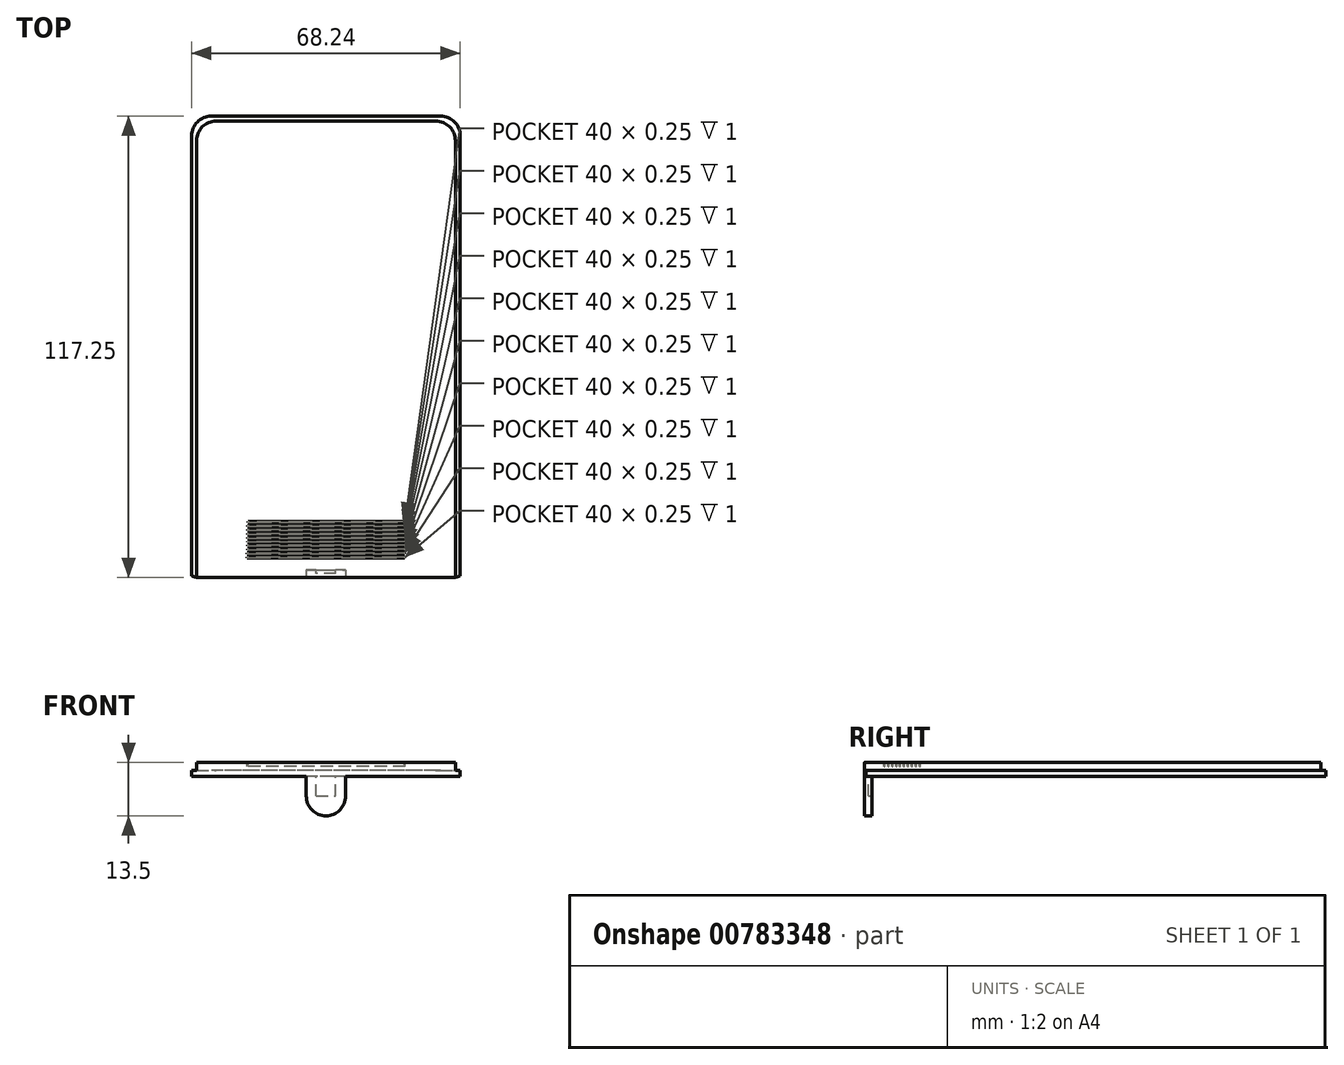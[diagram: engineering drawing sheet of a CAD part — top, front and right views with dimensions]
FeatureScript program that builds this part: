
annotation { "Feature Type Name" : "Feature", "Feature Type Description" : "" }
export const myFeature = defineFeature(function(context is Context, id is Id, definition is map)
    precondition{}
    {
        {
            var Q0;
            Q0=qCreatedBy(makeId("Front.planeOp"),FACE);
            var sketch = newSketch(context, id + "F0", { "sketchPlane" : qUnion([Q0])});
            skLineSegment(sketch, "E0.top", {"start": v(32.88, 3.5) * mm, "end": v(-32.87, 3.5) * mm});
            skLineSegment(sketch, "E0.left", {"start": v(32.88, 1.5) * mm, "end": v(32.88, 3.5) * mm});
            skLineSegment(sketch, "E0.right", {"start": v(-32.87, 1.5) * mm, "end": v(-32.87, 3.5) * mm});
            skLineSegment(sketch, "E1.bottom", {"start": v(34.12, 0) * mm, "end": v(-34.12, 0) * mm});
            skLineSegment(sketch, "E1.left", {"start": v(34.13, 0) * mm, "end": v(34.13, 1.5) * mm});
            skLineSegment(sketch, "E1.right", {"start": v(-34.12, 0) * mm, "end": v(-34.12, 1.5) * mm});
            skLineSegment(sketch, "E2", {"start": v(0, 3.25) * mm, "end": v(0, 44.31) * mm, "construction": true});
            skLineSegment(sketch, "E3", {"start": v(-34.12, 1.5) * mm, "end": v(-32.87, 1.5) * mm});
            skLineSegment(sketch, "E4", {"start": v(32.88, 1.5) * mm, "end": v(34.13, 1.5) * mm});
            skSolve(sketch);
        }
        {
            var Q0;
            Q0=makeQuery(id+"F0.imprint","IMPRINT",FACE,{"disambiguationData":[TD([[makeQuery(id+"F0.imprint","IMPRINT",EDGE,{"derivedFrom":sQuery(id+"F0.wireOp",EDGE,"E0.top")}),1.0]])]});
            extrude(context, id + "F1", {"entities" : qUnion([Q0]), "oppositeDirection" : true, "depth" : (106 + 10) * mm, "offsetDistance" : 25 * mm});
        }
        {
            var Q0;
            Q0=makeQuery(id+"F1.opExtrude","CAP_FACE",FACE,{"disambiguationData":[OSD([sQuery(id+"F0.wireOp",EDGE,"E0.top"),sQuery(id+"F0.wireOp",EDGE,"E0.left"),sQuery(id+"F0.wireOp",EDGE,"E0.right"),sQuery(id+"F0.wireOp",EDGE,"E1.bottom"),sQuery(id+"F0.wireOp",EDGE,"E1.left"),sQuery(id+"F0.wireOp",EDGE,"E1.right"),sQuery(id+"F0.wireOp",EDGE,"E3"),sQuery(id+"F0.wireOp",EDGE,"E4")])],"isStart":false});
            var sketch = newSketch(context, id + "F2", { "sketchPlane" : qUnion([Q0])});
            skLineSegment(sketch, "E5.bottom", {"start": v(-34.13, 1.5) * mm, "end": v(34.12, 1.5) * mm});
            skLineSegment(sketch, "E5.top", {"start": v(-34.13, 0) * mm, "end": v(34.12, 0) * mm});
            skLineSegment(sketch, "E5.left", {"start": v(-34.13, 1.5) * mm, "end": v(-34.13, 0) * mm});
            skLineSegment(sketch, "E5.right", {"start": v(34.12, 1.5) * mm, "end": v(34.12, 0) * mm});
            skSolve(sketch);
        }
        {
            var Q0;
            Q0=qSketchRegion(id+"F2",true);
            extrude(context, id + "F3", {"entities" : qUnion([Q0]), "operationType" : NewBodyOperationType.ADD, "depth" : 1.25 * mm, "offsetDistance" : 25 * mm});
        }
        {
            var Q0;
            Q0=makeQuery(id+"F3.opExtrude","CAP_EDGE",EDGE,{"disambiguationData":[OSD([sQuery(id+"F2.wireOp",EDGE,"E5.left")])],"isStart":false});
            var Q1;
            Q1=makeQuery(id+"F3.opExtrude","CAP_EDGE",EDGE,{"disambiguationData":[OSD([sQuery(id+"F2.wireOp",EDGE,"E5.right")])],"isStart":false});
            var Q2;
            Q2=makeQuery(id+"F1.opExtrude","CAP_EDGE",EDGE,{"disambiguationData":[OSD([sQuery(id+"F0.wireOp",EDGE,"E0.right")])],"isStart":false});
            var Q3;
            Q3=makeQuery(id+"F1.opExtrude","CAP_EDGE",EDGE,{"disambiguationData":[OSD([sQuery(id+"F0.wireOp",EDGE,"E0.left")])],"isStart":false});
            fillet(context, id + "F4", {"entities" : qUnion([Q0, Q1, Q2, Q3]), "radius" : 5 * mm, "tangentPropagation" : true, "allowEdgeOverflow" : false});
        }
        {
            var Q0;
            Q0=qCreatedBy(makeId("Top.planeOp"),FACE);
            var sketch = newSketch(context, id + "F5", { "sketchPlane" : qUnion([Q0])});
            skLineSegment(sketch, "E6.0.0", {"start": v(-34.12, 73) * mm, "end": v(34.12, 73) * mm, "construction": true});
            skLineSegment(sketch, "E6.0.1", {"start": v(34.12, 73) * mm, "end": v(34.12, 5) * mm, "construction": true});
            skLineSegment(sketch, "E6.0.2", {"start": v(29.12, 0) * mm, "end": v(-29.12, 0) * mm, "construction": true});
            skLineSegment(sketch, "E6.0.3", {"start": v(-34.12, 5) * mm, "end": v(-34.12, 73) * mm, "construction": true});
            skPoint(sketch, "E7.middle", {"position": v(-2.88, 36.5) * mm});
            skPoint(sketch, "E8.visualSharp", {"position": v(-37, 0) * mm});
            skArc(sketch, "E8.filletArc", {"start": v(-37, 5) * mm, "mid": v(-35.54, 1.46) * mm, "end": v(-32, 0) * mm, "construction": true});
            skPoint(sketch, "E9.visualSharp", {"position": v(37, 0) * mm});
            skArc(sketch, "E9.filletArc", {"start": v(32, 0) * mm, "mid": v(35.54, 1.46) * mm, "end": v(37, 5) * mm, "construction": true});
            skArc(sketch, "E10", {"start": v(-37, 5) * mm, "mid": v(-35.54, 1.46) * mm, "end": v(-32, 0) * mm});
            skLineSegment(sketch, "E11", {"start": v(-32.48, -8.24) * mm, "end": v(-32, 0) * mm});
            skLineSegment(sketch, "E12", {"start": v(-37, 5) * mm, "end": v(-47.45, 5.13) * mm});
            skLineSegment(sketch, "E13", {"start": v(0, 0) * mm, "end": v(0, 9.43) * mm, "construction": true});
            skLineSegment(sketch, "E14.MirrorCS", {"start": v(37, 5) * mm, "end": v(47.87, 4.85) * mm});
            skLineSegment(sketch, "E15.MirrorCS", {"start": v(31.7, -9.05) * mm, "end": v(32, 0) * mm});
            skPoint(sketch, "E16.MirrorP", {"position": v(31.25, 0) * mm});
            skLineSegment(sketch, "E17", {"start": v(-47.45, 5.13) * mm, "end": v(-32.48, -8.24) * mm});
            skLineSegment(sketch, "E18", {"start": v(31.7, -9.05) * mm, "end": v(47.87, 4.85) * mm});
            skArc(sketch, "E19.MirrorCS", {"start": v(37, 5) * mm, "mid": v(35.54, 1.46) * mm, "end": v(32, 0) * mm});
            skArc(sketch, "E20.MirrorCS", {"start": v(37, 5) * mm, "mid": v(35.54, 1.46) * mm, "end": v(32, 0) * mm, "construction": true});
            skSolve(sketch);
        }
        {
            var Q0;
            Q0=qSketchRegion(id+"F5",true);
            extrude(context, id + "F6", {"entities" : qUnion([Q0]), "operationType" : NewBodyOperationType.REMOVE, "depth" : 25 * mm, "offsetDistance" : 25 * mm});
        }
        {
            var Q0;
            Q0=makeQuery(id+"F1.opExtrude","CAP_FACE",FACE,{"disambiguationData":[OSD([sQuery(id+"F0.wireOp",EDGE,"E0.top"),sQuery(id+"F0.wireOp",EDGE,"E0.left"),sQuery(id+"F0.wireOp",EDGE,"E0.right"),sQuery(id+"F0.wireOp",EDGE,"E1.bottom"),sQuery(id+"F0.wireOp",EDGE,"E1.left"),sQuery(id+"F0.wireOp",EDGE,"E1.right"),sQuery(id+"F0.wireOp",EDGE,"E3"),sQuery(id+"F0.wireOp",EDGE,"E4")])],"isStart":true});
            var sketch = newSketch(context, id + "F7", { "sketchPlane" : qUnion([Q0])});
            skLineSegment(sketch, "E21.bottom", {"start": v(5, -10) * mm, "end": v(-5, -10) * mm});
            skLineSegment(sketch, "E21.top", {"start": v(5, 0) * mm, "end": v(-5, 0) * mm});
            skLineSegment(sketch, "E21.left", {"start": v(5, -10) * mm, "end": v(5, 0) * mm});
            skLineSegment(sketch, "E21.right", {"start": v(-5, -10) * mm, "end": v(-5, 0) * mm});
            skPoint(sketch, "E21.middle", {"position": v(0, -5) * mm});
            skSolve(sketch);
        }
        {
            var Q0;
            Q0=qSketchRegion(id+"F7",true);
            extrude(context, id + "F8", {"entities" : qUnion([Q0]), "operationType" : NewBodyOperationType.ADD, "oppositeDirection" : true, "depth" : 2 * mm, "offsetDistance" : 25 * mm});
        }
        {
            var Q0;
            Q0=makeQuery(id+"F8.opExtrude","SWEPT_EDGE",EDGE,{"disambiguationData":[OSD([sQuery(id+"F0.wireOp",EDGE,"E1.bottom"),sQuery(id+"F7.wireOp",EDGE,"E21.top"),sQuery(id+"F7.wireOp",EDGE,"E21.left")])]});
            var Q1;
            Q1=makeQuery(id+"F8.opExtrude","SWEPT_EDGE",EDGE,{"disambiguationData":[OSD([sQuery(id+"F0.wireOp",EDGE,"E1.bottom"),sQuery(id+"F7.wireOp",EDGE,"E21.top"),sQuery(id+"F7.wireOp",EDGE,"E21.right")])]});
            var Q2;
            Q2=makeQuery(id+"F8.opExtrude","SWEPT_EDGE",EDGE,{"disambiguationData":[OSD([sQuery(id+"F7.wireOp",EDGE,"E21.bottom"),sQuery(id+"F7.wireOp",EDGE,"E21.right")])]});
            var Q3;
            Q3=makeQuery(id+"F8.opExtrude","SWEPT_EDGE",EDGE,{"disambiguationData":[OSD([sQuery(id+"F7.wireOp",EDGE,"E21.bottom"),sQuery(id+"F7.wireOp",EDGE,"E21.left")])]});
            fillet(context, id + "F9", {"entities" : qUnion([Q0, Q1, Q2, Q3]), "radius" : 5 * mm, "tangentPropagation" : true, "allowEdgeOverflow" : false});
        }
        {
            var Q0;
            Q0=makeQuery(id+"F8.opExtrude","CAP_FACE",FACE,{"disambiguationData":[OSD([sQuery(id+"F7.wireOp",EDGE,"E21.bottom"),sQuery(id+"F7.wireOp",EDGE,"E21.top"),sQuery(id+"F7.wireOp",EDGE,"E21.left"),sQuery(id+"F7.wireOp",EDGE,"E21.right")])],"isStart":false});
            var sketch = newSketch(context, id + "F10", { "sketchPlane" : qUnion([Q0])});
            skLineSegment(sketch, "E22.bottom", {"start": v(2.5, -5) * mm, "end": v(-2.5, -5) * mm});
            skLineSegment(sketch, "E22.top", {"start": v(2.5, 0) * mm, "end": v(-2.5, 0) * mm});
            skLineSegment(sketch, "E22.left", {"start": v(2.5, -5) * mm, "end": v(2.5, 0) * mm});
            skLineSegment(sketch, "E22.right", {"start": v(-2.5, -5) * mm, "end": v(-2.5, 0) * mm});
            skPoint(sketch, "E22.middle", {"position": v(0, -2.5) * mm});
            skPoint(sketch, "E23", {"position": v(0, 0) * mm});
            skSolve(sketch);
        }
        {
            var Q0;
            Q0=qSketchRegion(id+"F10",true);
            extrude(context, id + "F11", {"entities" : qUnion([Q0]), "operationType" : NewBodyOperationType.REMOVE, "oppositeDirection" : true, "depth" : 1 * mm, "offsetDistance" : 25 * mm});
        }
        {
            var Q0;
            Q0=makeQuery(id+"F1.opExtrude","SWEPT_FACE",FACE,{"disambiguationData":[OSD([sQuery(id+"F0.wireOp",EDGE,"E0.top")])]});
            var sketch = newSketch(context, id + "F12", { "sketchPlane" : qUnion([Q0])});
            skLineSegment(sketch, "E24.bottom", {"start": v(20, 5) * mm, "end": v(-20, 5) * mm});
            skLineSegment(sketch, "E24.top", {"start": v(20, 5.25) * mm, "end": v(-20, 5.25) * mm});
            skLineSegment(sketch, "E24.left", {"start": v(20, 5) * mm, "end": v(20, 5.25) * mm});
            skLineSegment(sketch, "E24.right", {"start": v(-20, 5) * mm, "end": v(-20, 5.25) * mm});
            skPoint(sketch, "E24.middle", {"position": v(0, 5.13) * mm});
            skLineSegment(sketch, "E25", {"start": v(0, 0) * mm, "end": v(0, 5) * mm, "construction": true});
            skPoint(sketch, "E26.0.1.0", {"position": v(0.02, 6.12) * mm});
            skLineSegment(sketch, "E26.0.1.1", {"start": v(20.02, 6.25) * mm, "end": v(-19.98, 6.25) * mm});
            skLineSegment(sketch, "E26.0.1.2", {"start": v(20.02, 6) * mm, "end": v(-19.98, 6) * mm});
            skLineSegment(sketch, "E26.0.1.3", {"start": v(20.02, 6) * mm, "end": v(20.02, 6.25) * mm});
            skLineSegment(sketch, "E26.0.1.4", {"start": v(-19.98, 6) * mm, "end": v(-19.98, 6.25) * mm});
            skPoint(sketch, "E26.0.2.0", {"position": v(0.03, 7.12) * mm});
            skLineSegment(sketch, "E26.0.2.1", {"start": v(20.03, 7.25) * mm, "end": v(-19.97, 7.25) * mm});
            skLineSegment(sketch, "E26.0.2.2", {"start": v(20.03, 7) * mm, "end": v(-19.97, 7) * mm});
            skLineSegment(sketch, "E26.0.2.3", {"start": v(20.03, 7) * mm, "end": v(20.03, 7.25) * mm});
            skLineSegment(sketch, "E26.0.2.4", {"start": v(-19.97, 7) * mm, "end": v(-19.97, 7.25) * mm});
            skPoint(sketch, "E26.0.3.0", {"position": v(0.05, 8.12) * mm});
            skLineSegment(sketch, "E26.0.3.1", {"start": v(20.05, 8.25) * mm, "end": v(-19.95, 8.25) * mm});
            skLineSegment(sketch, "E26.0.3.2", {"start": v(20.05, 8) * mm, "end": v(-19.95, 8) * mm});
            skLineSegment(sketch, "E26.0.3.3", {"start": v(20.05, 8) * mm, "end": v(20.05, 8.25) * mm});
            skLineSegment(sketch, "E26.0.3.4", {"start": v(-19.95, 8) * mm, "end": v(-19.95, 8.25) * mm});
            skPoint(sketch, "E26.0.4.0", {"position": v(0.07, 9.12) * mm});
            skLineSegment(sketch, "E26.0.4.1", {"start": v(20.07, 9.25) * mm, "end": v(-19.93, 9.25) * mm});
            skLineSegment(sketch, "E26.0.4.2", {"start": v(20.07, 9) * mm, "end": v(-19.93, 9) * mm});
            skLineSegment(sketch, "E26.0.4.3", {"start": v(20.07, 9) * mm, "end": v(20.07, 9.25) * mm});
            skLineSegment(sketch, "E26.0.4.4", {"start": v(-19.93, 9) * mm, "end": v(-19.93, 9.25) * mm});
            skPoint(sketch, "E26.0.5.0", {"position": v(0.08, 10.12) * mm});
            skLineSegment(sketch, "E26.0.5.1", {"start": v(20.08, 10.25) * mm, "end": v(-19.92, 10.25) * mm});
            skLineSegment(sketch, "E26.0.5.2", {"start": v(20.08, 10) * mm, "end": v(-19.92, 10) * mm});
            skLineSegment(sketch, "E26.0.5.3", {"start": v(20.08, 10) * mm, "end": v(20.08, 10.25) * mm});
            skLineSegment(sketch, "E26.0.5.4", {"start": v(-19.92, 10) * mm, "end": v(-19.92, 10.25) * mm});
            skPoint(sketch, "E26.0.6.0", {"position": v(0.1, 11.12) * mm});
            skLineSegment(sketch, "E26.0.6.1", {"start": v(20.1, 11.25) * mm, "end": v(-19.9, 11.25) * mm});
            skLineSegment(sketch, "E26.0.6.2", {"start": v(20.1, 11) * mm, "end": v(-19.9, 11) * mm});
            skLineSegment(sketch, "E26.0.6.3", {"start": v(20.1, 11) * mm, "end": v(20.1, 11.25) * mm});
            skLineSegment(sketch, "E26.0.6.4", {"start": v(-19.9, 11) * mm, "end": v(-19.9, 11.25) * mm});
            skPoint(sketch, "E26.0.7.0", {"position": v(0.12, 12.12) * mm});
            skLineSegment(sketch, "E26.0.7.1", {"start": v(20.12, 12.25) * mm, "end": v(-19.88, 12.25) * mm});
            skLineSegment(sketch, "E26.0.7.2", {"start": v(20.12, 12) * mm, "end": v(-19.88, 12) * mm});
            skLineSegment(sketch, "E26.0.7.3", {"start": v(20.12, 12) * mm, "end": v(20.12, 12.25) * mm});
            skLineSegment(sketch, "E26.0.7.4", {"start": v(-19.88, 12) * mm, "end": v(-19.88, 12.25) * mm});
            skPoint(sketch, "E26.0.8.0", {"position": v(0.14, 13.12) * mm});
            skLineSegment(sketch, "E26.0.8.1", {"start": v(20.14, 13.25) * mm, "end": v(-19.86, 13.25) * mm});
            skLineSegment(sketch, "E26.0.8.2", {"start": v(20.14, 13) * mm, "end": v(-19.86, 13) * mm});
            skLineSegment(sketch, "E26.0.8.3", {"start": v(20.14, 13) * mm, "end": v(20.14, 13.25) * mm});
            skLineSegment(sketch, "E26.0.8.4", {"start": v(-19.86, 13) * mm, "end": v(-19.86, 13.25) * mm});
            skPoint(sketch, "E26.0.9.0", {"position": v(0.15, 14.12) * mm});
            skLineSegment(sketch, "E26.0.9.1", {"start": v(20.15, 14.25) * mm, "end": v(-19.85, 14.25) * mm});
            skLineSegment(sketch, "E26.0.9.2", {"start": v(20.15, 14) * mm, "end": v(-19.85, 14) * mm});
            skLineSegment(sketch, "E26.0.9.3", {"start": v(20.15, 14) * mm, "end": v(20.15, 14.25) * mm});
            skLineSegment(sketch, "E26.0.9.4", {"start": v(-19.85, 14) * mm, "end": v(-19.85, 14.25) * mm});
            skLineSegment(sketch, "E26.direction1", {"start": v(-20, 5) * mm, "end": v(5, 5) * mm, "construction": true});
            skLineSegment(sketch, "E26.direction2", {"start": v(-20, 5) * mm, "end": v(-19.98, 6) * mm, "construction": true});
            skSolve(sketch);
        }
        {
            var Q0;
            Q0=qSketchRegion(id+"F12",true);
            extrude(context, id + "F13", {"entities" : qUnion([Q0]), "operationType" : NewBodyOperationType.REMOVE, "oppositeDirection" : true, "depth" : 1 * mm, "offsetDistance" : 25 * mm});
        }
    });
